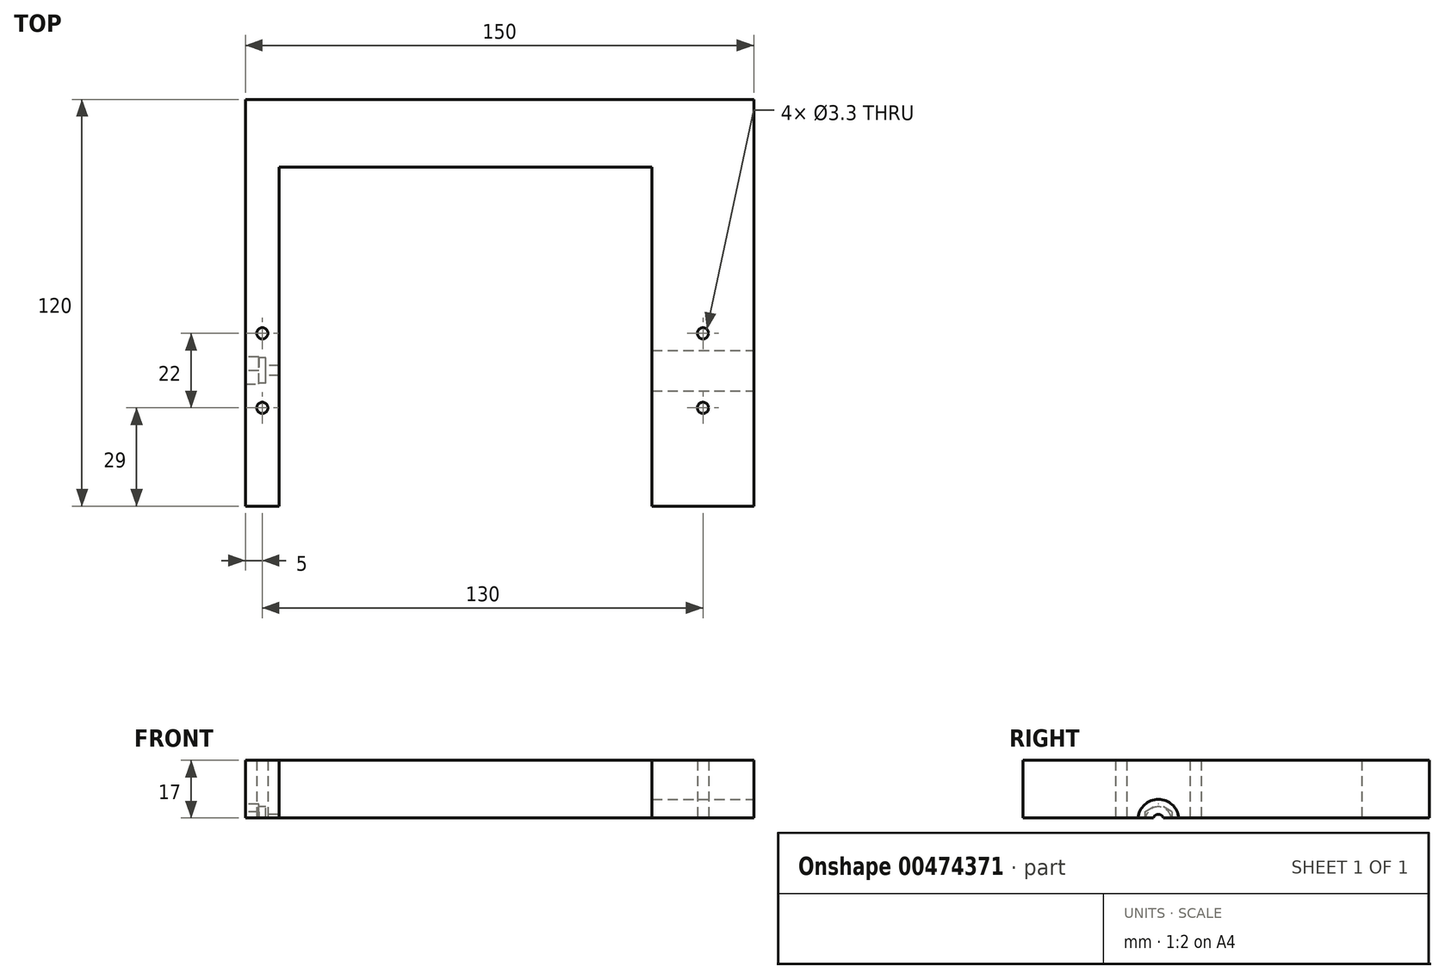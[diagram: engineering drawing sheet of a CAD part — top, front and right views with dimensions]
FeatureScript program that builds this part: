
annotation { "Feature Type Name" : "Feature", "Feature Type Description" : "" }
export const myFeature = defineFeature(function(context is Context, id is Id, definition is map)
    precondition{}
    {
        {
            var Q0;
            Q0=qCreatedBy(makeId("Top.planeOp"),FACE);
            var sketch = newSketch(context, id + "F0", { "sketchPlane" : qUnion([Q0])});
            skLineSegment(sketch, "E0.bottom", {"start": v(-75, -60) * mm, "end": v(75, -60) * mm});
            skLineSegment(sketch, "E0.top", {"start": v(-75, 60) * mm, "end": v(75, 60) * mm});
            skLineSegment(sketch, "E0.left", {"start": v(-75, -60) * mm, "end": v(-75, 60) * mm});
            skLineSegment(sketch, "E0.right", {"start": v(75, -60) * mm, "end": v(75, 60) * mm});
            skPoint(sketch, "E0.middle", {"position": v(0, 0) * mm});
            skSolve(sketch);
        }
        {
            var Q0;
            Q0=qSketchRegion(id+"F0",true);
            extrude(context, id + "F1", {"entities" : qUnion([Q0]), "depth" : 30 * mm});
        }
        {
            var Q0;
            Q0=makeQuery(id+"F1.opExtrude","SWEPT_FACE",FACE,{"disambiguationData":[OSD([sQuery(id+"F0.wireOp",EDGE,"E0.left")])]});
            var sketch = newSketch(context, id + "F2", { "sketchPlane" : qUnion([Q0])});
            skPoint(sketch, "E1.endSnap0", {"position": v(0, 0) * mm});
            skLineSegment(sketch, "E2", {"start": v(-60, 15) * mm, "end": v(-40, 15) * mm, "construction": true});
            skLineSegment(sketch, "E3", {"start": v(60, 0) * mm, "end": v(60, 12.5) * mm, "construction": true});
            skLineSegment(sketch, "E4", {"start": v(60, 12.5) * mm, "end": v(20, 12.5) * mm, "construction": true});
            skLineSegment(sketch, "E5", {"start": v(20, 12.5) * mm, "end": v(20, 17.12) * mm, "construction": true});
            skLineSegment(sketch, "E6", {"start": v(20, 12.5) * mm, "end": v(24, 14.8) * mm, "construction": true});
            skLineSegment(sketch, "E7.MirrorCS", {"start": v(20, 12.5) * mm, "end": v(24, 10.19) * mm, "construction": true});
            skLineSegment(sketch, "E8.MirrorCS", {"start": v(20, 12.5) * mm, "end": v(20, 7.88) * mm, "construction": true});
            skLineSegment(sketch, "E9.MirrorCS", {"start": v(20, 12.5) * mm, "end": v(16, 10.19) * mm, "construction": true});
            skLineSegment(sketch, "E10.MirrorCS", {"start": v(20, 12.5) * mm, "end": v(16, 14.8) * mm, "construction": true});
            skLineSegment(sketch, "E11", {"start": v(16, 14.8) * mm, "end": v(20, 17.12) * mm});
            skLineSegment(sketch, "E12", {"start": v(16, 14.8) * mm, "end": v(16, 10.19) * mm});
            skLineSegment(sketch, "E13", {"start": v(16, 10.19) * mm, "end": v(20, 7.88) * mm});
            skLineSegment(sketch, "E14", {"start": v(20, 7.88) * mm, "end": v(24, 10.2) * mm});
            skLineSegment(sketch, "E15", {"start": v(24, 14.8) * mm, "end": v(24, 10.19) * mm});
            skLineSegment(sketch, "E16", {"start": v(24, 14.8) * mm, "end": v(20, 17.12) * mm});
            skLineSegment(sketch, "E17", {"start": v(16, 14.8) * mm, "end": v(24, 14.8) * mm, "construction": true});
            skSolve(sketch);
        }
        {
            var Q0;
            Q0=qCreatedBy(makeId("Top.planeOp"),FACE);
            var sketch = newSketch(context, id + "F3", { "sketchPlane" : qUnion([Q0])});
            skLineSegment(sketch, "E18.bottom", {"start": v(75, -60) * mm, "end": v(-75, -60) * mm, "construction": true});
            skLineSegment(sketch, "E18.top", {"start": v(75, 60) * mm, "end": v(-75, 60) * mm, "construction": true});
            skLineSegment(sketch, "E18.left", {"start": v(75, -60) * mm, "end": v(75, 60) * mm, "construction": true});
            skLineSegment(sketch, "E18.right", {"start": v(-75, -60) * mm, "end": v(-75, 60) * mm, "construction": true});
            skPoint(sketch, "E18.middle", {"position": v(0, 0) * mm});
            skLineSegment(sketch, "E19", {"start": v(75, -60) * mm, "end": v(45, -60) * mm, "construction": true});
            skLineSegment(sketch, "E20", {"start": v(45, -60) * mm, "end": v(45, 40) * mm});
            skLineSegment(sketch, "E21", {"start": v(45, 40) * mm, "end": v(-65, 40) * mm});
            skLineSegment(sketch, "E22", {"start": v(-65, 40) * mm, "end": v(-65, -60) * mm});
            skLineSegment(sketch, "E23", {"start": v(-75, -60) * mm, "end": v(-65, -60) * mm, "construction": true});
            skLineSegment(sketch, "E24", {"start": v(-65, -60) * mm, "end": v(45, -60) * mm});
            skSolve(sketch);
        }
        {
            var Q0;
            Q0 = qSketchRegion(id + "F3", true);
            var Q1;
            Q1=makeQuery(id+"F1.opExtrude","CAP_FACE",FACE,{"disambiguationData":[OSD([sQuery(id+"F0.wireOp",EDGE,"E0.bottom"),sQuery(id+"F0.wireOp",EDGE,"E0.top"),sQuery(id+"F0.wireOp",EDGE,"E0.left"),sQuery(id+"F0.wireOp",EDGE,"E0.right")])],"isStart":false});
            extrude(context, id + "F4", {"entities" : qUnion([Q0]), "operationType" : NewBodyOperationType.REMOVE, "endBound" : BoundingType.UP_TO_SURFACE, "endBoundEntityFace" : qUnion([Q1]), "depth" : 25 * mm});
        }
        {
            var Q0;
            Q0=qSketchRegion(id+"F2",true);
            extrude(context, id + "F5", {"entities" : qUnion([Q0]), "operationType" : NewBodyOperationType.REMOVE, "oppositeDirection" : true, "depth" : 4 * mm});
        }
        {
            var Q0;
            Q0=makeQuery(id+"F5.boolean.opBoolean","COPY",FACE,{"derivedFrom":makeQuery(id+"F5.opExtrude","CAP_FACE",FACE,{"disambiguationData":[OSD([sQuery(id+"F2.wireOp",EDGE,"E11"),sQuery(id+"F2.wireOp",EDGE,"E12"),sQuery(id+"F2.wireOp",EDGE,"E13"),sQuery(id+"F2.wireOp",EDGE,"E14"),sQuery(id+"F2.wireOp",EDGE,"E15"),sQuery(id+"F2.wireOp",EDGE,"E16")])],"isStart":false})});
            var sketch = newSketch(context, id + "F6", { "sketchPlane" : qUnion([Q0])});
            skCircle(sketch, "E25", {"center": v(20, 12.5) * mm, "radius": 3.8 * mm});
            skLineSegment(sketch, "E26", {"start": v(20, 17.12) * mm, "end": v(20, 7.88) * mm, "construction": true});
            skLineSegment(sketch, "E27", {"start": v(16, 10.19) * mm, "end": v(24, 14.8) * mm, "construction": true});
            skSolve(sketch);
        }
        {
            var Q0;
            Q0=qSketchRegion(id+"F6",true);
            extrude(context, id + "F7", {"entities" : qUnion([Q0]), "operationType" : NewBodyOperationType.REMOVE, "oppositeDirection" : true, "depth" : 2 * mm});
        }
        {
            var Q0;
            Q0=makeQuery(id+"F7.boolean.opBoolean","COPY",FACE,{"derivedFrom":makeQuery(id+"F7.opExtrude","CAP_FACE",FACE,{"disambiguationData":[OSD([sQuery(id+"F6.wireOp",EDGE,"E25")])],"isStart":false})});
            var sketch = newSketch(context, id + "F8", { "sketchPlane" : qUnion([Q0])});
            skCircle(sketch, "E28", {"center": v(20, 12.5) * mm, "radius": 1.55 * mm});
            skSolve(sketch);
        }
        {
            var Q0;
            Q0=qSketchRegion(id+"F8",true);
            extrude(context, id + "F9", {"entities" : qUnion([Q0]), "operationType" : NewBodyOperationType.REMOVE, "oppositeDirection" : true, "depth" : 7 * mm});
        }
        {
            var Q0;
            Q0=makeQuery(id+"F1.opExtrude","SWEPT_FACE",FACE,{"disambiguationData":[OSD([sQuery(id+"F0.wireOp",EDGE,"E0.right")])]});
            var sketch = newSketch(context, id + "F10", { "sketchPlane" : qUnion([Q0])});
            skLineSegment(sketch, "E29", {"start": v(-60, 0) * mm, "end": v(-60, 12.5) * mm, "construction": true});
            skLineSegment(sketch, "E30", {"start": v(-60, 12.5) * mm, "end": v(-20, 12.5) * mm, "construction": true});
            skCircle(sketch, "E31", {"center": v(-20, 12.5) * mm, "radius": 6 * mm});
            skSolve(sketch);
        }
        {
            var Q0;
            Q0=makeQuery(id+"F1.opExtrude","SWEPT_FACE",FACE,{"disambiguationData":[OSD([sQuery(id+"F0.wireOp",EDGE,"E0.top")])]});
            var sketch = newSketch(context, id + "F11", { "sketchPlane" : qUnion([Q0])});
            skPoint(sketch, "E32.endSnap0", {"position": v(0, 0) * mm});
            skLineSegment(sketch, "E33", {"start": v(-75, 6) * mm, "end": v(-50, 6) * mm, "construction": true});
            skPoint(sketch, "E34", {"position": v(-50, 6) * mm});
            skLineSegment(sketch, "E35", {"start": v(75, 6) * mm, "end": v(65, 6) * mm, "construction": true});
            skLineSegment(sketch, "E36", {"start": v(-5, 6) * mm, "end": v(20, 6) * mm, "construction": true});
            skCircle(sketch, "E37", {"center": v(20, 6) * mm, "radius": 0.5 * mm});
            skLineSegment(sketch, "E38", {"start": v(20, 6) * mm, "end": v(65, 6) * mm, "construction": true});
            skLineSegment(sketch, "E39", {"start": v(0, 0) * mm, "end": v(-5, 0) * mm, "construction": true});
            skLineSegment(sketch, "E40", {"start": v(0, 0) * mm, "end": v(0, 6) * mm, "construction": true});
            skCircle(sketch, "E41", {"center": v(-5, 6) * mm, "radius": 0.5 * mm});
            skLineSegment(sketch, "E42", {"start": v(-50, 6) * mm, "end": v(-5, 6) * mm, "construction": true});
            skSolve(sketch);
        }
        {
            var Q0;
            Q0=makeQuery(id+"F10.imprint","IMPRINT",FACE,{"disambiguationData":[TD([[makeQuery(id+"F10.imprint","IMPRINT",EDGE,{"derivedFrom":sQuery(id+"F10.wireOp",EDGE,"E31")}),1.0]])]});
            var Q1;
            Q1=makeQuery(id+"F4.boolean.opBoolean","COPY",FACE,{"derivedFrom":makeQuery(id+"F4.opExtrude","SWEPT_FACE",FACE,{"disambiguationData":[OSD([sQuery(id+"F3.wireOp",EDGE,"E20")])]})});
            extrude(context, id + "F12", {"entities" : qUnion([Q0]), "operationType" : NewBodyOperationType.REMOVE, "endBound" : BoundingType.UP_TO_SURFACE, "oppositeDirection" : true, "endBoundEntityFace" : qUnion([Q1]), "depth" : 25 * mm});
        }
        {
            var Q0;
            Q0=qSketchRegion(id+"F11",true);
            var Q1;
            Q1=makeQuery(id+"F4.boolean.opBoolean","COPY",FACE,{"derivedFrom":makeQuery(id+"F4.opExtrude","SWEPT_FACE",FACE,{"disambiguationData":[OSD([sQuery(id+"F3.wireOp",EDGE,"YkLpMczh-LnJE-8Oms-Y8Ta-dxZD4QefJqg7")])]})});
            extrude(context, id + "F13", {"entities" : qUnion([Q0]), "operationType" : NewBodyOperationType.REMOVE, "oppositeDirection" : true, "endBoundEntityFace" : qUnion([Q1]), "depth" : 1 * mm});
        }
        {
            var Q0;
            Q0=qCreatedBy(makeId("Top.planeOp"),FACE);
            var sketch = newSketch(context, id + "F14", { "sketchPlane" : qUnion([Q0])});
            skLineSegment(sketch, "E43.bottom", {"start": v(75, 60) * mm, "end": v(-75, 60) * mm});
            skLineSegment(sketch, "E43.top", {"start": v(75, -60) * mm, "end": v(-75, -60) * mm});
            skLineSegment(sketch, "E43.left", {"start": v(75, 60) * mm, "end": v(75, -60) * mm});
            skLineSegment(sketch, "E43.right", {"start": v(-75, 60) * mm, "end": v(-75, -60) * mm});
            skPoint(sketch, "E43.middle", {"position": v(0, 0) * mm});
            skSolve(sketch);
        }
        {
            var Q0;
            Q0 = qSketchRegion(id + "F14", true);
            extrude(context, id + "F15", {"entities" : qUnion([Q0]), "operationType" : NewBodyOperationType.REMOVE, "depth" : 13 * mm});
        }
        {
            var Q0;
            Q0=qCreatedBy(makeId("Top.planeOp"),FACE);
            var sketch = newSketch(context, id + "F16", { "sketchPlane" : qUnion([Q0])});
            skPoint(sketch, "E44.middle", {"position": v(0, 0) * mm});
            skLineSegment(sketch, "E45.bottom", {"start": v(-75, -60) * mm, "end": v(75, -60) * mm, "construction": true});
            skLineSegment(sketch, "E45.top", {"start": v(-75, 60) * mm, "end": v(75, 60) * mm, "construction": true});
            skLineSegment(sketch, "E45.left", {"start": v(-75, -60) * mm, "end": v(-75, 60) * mm, "construction": true});
            skLineSegment(sketch, "E45.right", {"start": v(75, -60) * mm, "end": v(75, 60) * mm, "construction": true});
            skLineSegment(sketch, "E46", {"start": v(-75, -60) * mm, "end": v(-70, -60) * mm, "construction": true});
            skLineSegment(sketch, "E47", {"start": v(-70, -60) * mm, "end": v(-70, -20) * mm, "construction": true});
            skLineSegment(sketch, "E48", {"start": v(-70, -20) * mm, "end": v(60, -20) * mm, "construction": true});
            skLineSegment(sketch, "E49", {"start": v(60, -20) * mm, "end": v(60, -60) * mm, "construction": true});
            skLineSegment(sketch, "E50", {"start": v(-70, -20) * mm, "end": v(-70, -31) * mm, "construction": true});
            skLineSegment(sketch, "E51", {"start": v(-70, -20) * mm, "end": v(-70, -9) * mm, "construction": true});
            skCircle(sketch, "E52", {"center": v(-70, -9) * mm, "radius": 1.65 * mm});
            skCircle(sketch, "E53", {"center": v(-70, -31) * mm, "radius": 1.65 * mm});
            skLineSegment(sketch, "E54", {"start": v(60, -20) * mm, "end": v(60, -9) * mm, "construction": true});
            skLineSegment(sketch, "E55", {"start": v(60, -20) * mm, "end": v(60, -31) * mm, "construction": true});
            skCircle(sketch, "E56", {"center": v(60, -9) * mm, "radius": 1.65 * mm});
            skCircle(sketch, "E57", {"center": v(60, -31) * mm, "radius": 1.65 * mm});
            skSolve(sketch);
        }
        {
            var Q0;
            Q0 = qSketchRegion(id + "F16", true);
            var Q1;
            Q1=makeQuery(id+"F1.opExtrude","CAP_FACE",FACE,{"disambiguationData":[OSD([sQuery(id+"F0.wireOp",EDGE,"E0.bottom"),sQuery(id+"F0.wireOp",EDGE,"E0.top"),sQuery(id+"F0.wireOp",EDGE,"E0.left"),sQuery(id+"F0.wireOp",EDGE,"E0.right")])],"isStart":false});
            extrude(context, id + "F17", {"entities" : qUnion([Q0]), "operationType" : NewBodyOperationType.REMOVE, "endBound" : BoundingType.UP_TO_SURFACE, "endBoundEntityFace" : qUnion([Q1]), "depth" : 25 * mm});
        }
    });
